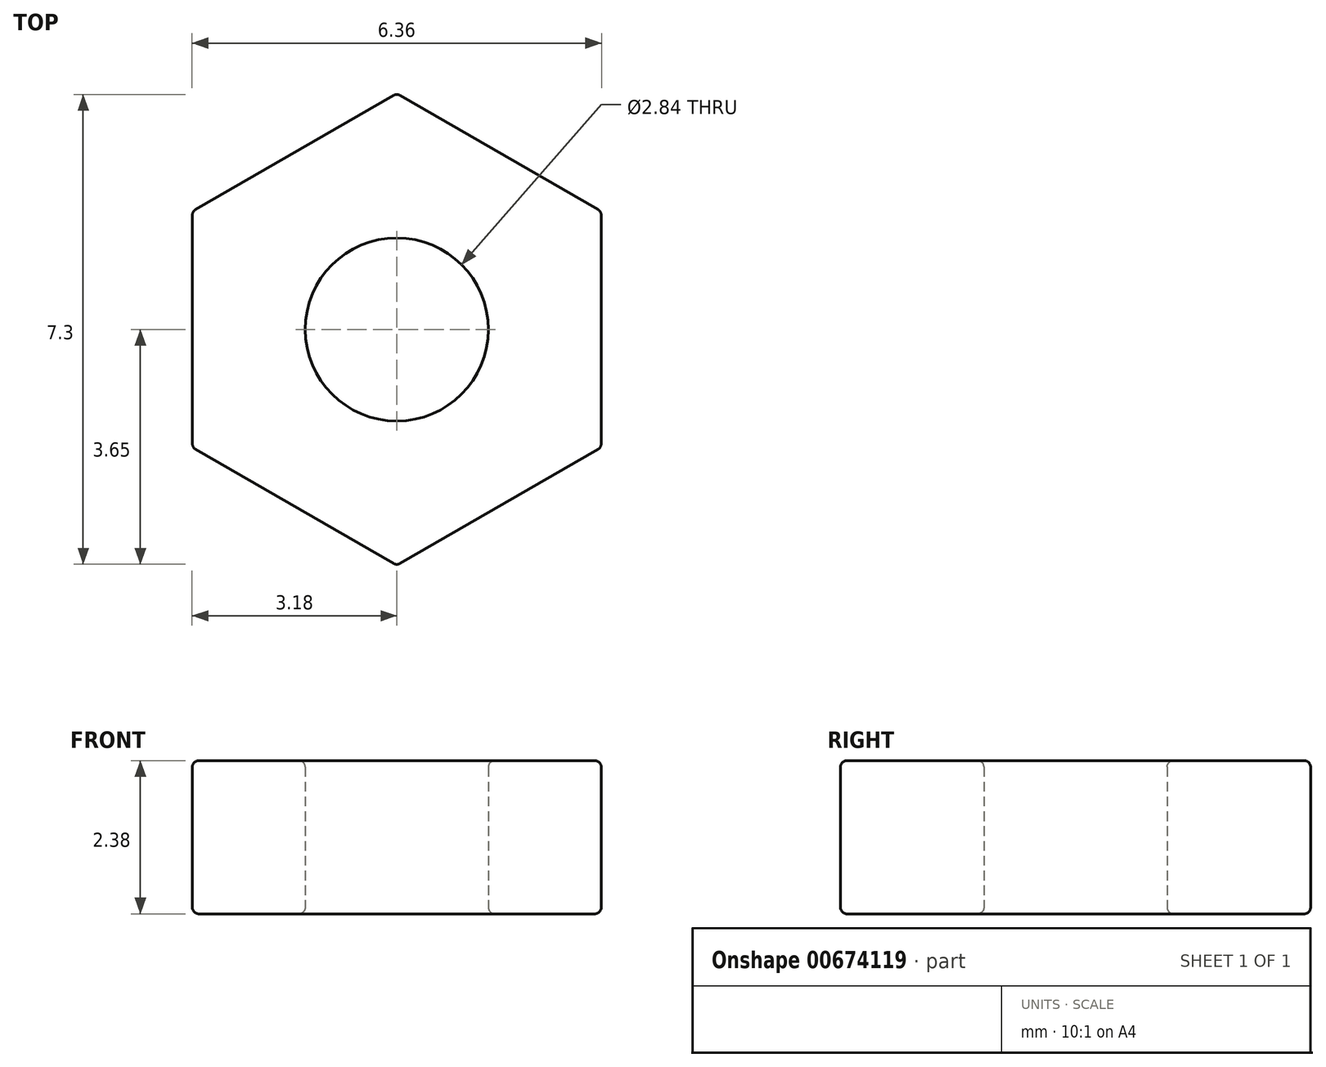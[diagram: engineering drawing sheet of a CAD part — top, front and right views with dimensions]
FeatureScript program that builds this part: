
annotation { "Feature Type Name" : "Feature", "Feature Type Description" : "" }
export const myFeature = defineFeature(function(context is Context, id is Id, definition is map)
    precondition{}
    {
        {
            var Q0;
            Q0=qCreatedBy(makeId("Top.planeOp"),FACE);
            var sketch = newSketch(context, id + "F0", { "sketchPlane" : qUnion([Q0])});
            skCircle(sketch, "E0", {"center": v(0, 0) * mm, "radius": 1.42 * mm});
            skCircle(sketch, "E1.cCircle", {"center": v(0, 0) * mm, "radius": 3.18 * mm, "construction": true});
            skLineSegment(sketch, "E1.0", {"start": v(3.18, 1.83) * mm, "end": v(3.18, -1.83) * mm});
            skLineSegment(sketch, "E1.1", {"start": v(3.18, -1.83) * mm, "end": v(0, -3.67) * mm});
            skLineSegment(sketch, "E1.2", {"start": v(0, -3.67) * mm, "end": v(-3.17, -1.83) * mm});
            skLineSegment(sketch, "E1.3", {"start": v(-3.17, -1.83) * mm, "end": v(-3.18, 1.83) * mm});
            skLineSegment(sketch, "E1.4", {"start": v(-3.18, 1.83) * mm, "end": v(0, 3.67) * mm});
            skLineSegment(sketch, "E1.5", {"start": v(0, 3.67) * mm, "end": v(3.18, 1.83) * mm});
            skPoint(sketch, "E1.0.midPoint", {"position": v(3.18, 0) * mm});
            skSolve(sketch);
        }
        {
            var Q0;
            Q0=makeQuery(id+"F0.imprint","IMPRINT",FACE,{"disambiguationData":[TD([[makeQuery(id+"F0.imprint","IMPRINT",EDGE,{"derivedFrom":sQuery(id+"F0.wireOp",EDGE,"E0")}),-1.0]])]});
            extrude(context, id + "F1", {"entities" : qUnion([Q0]), "depth" : 2.38 * mm, "offsetDistance" : 25 * mm});
        }
        {
            var Q0;
            Q0=makeQuery(id+"F1.opExtrude","SWEPT_FACE",FACE,{"disambiguationData":[OSD([sQuery(id+"F0.wireOp",EDGE,"E1.2")])]});
            var Q1;
            Q1=makeQuery(id+"F1.opExtrude","SWEPT_FACE",FACE,{"disambiguationData":[OSD([sQuery(id+"F0.wireOp",EDGE,"E1.1")])]});
            var Q2;
            Q2=makeQuery(id+"F1.opExtrude","SWEPT_FACE",FACE,{"disambiguationData":[OSD([sQuery(id+"F0.wireOp",EDGE,"E1.0")])]});
            var Q3;
            Q3=makeQuery(id+"F1.opExtrude","SWEPT_FACE",FACE,{"disambiguationData":[OSD([sQuery(id+"F0.wireOp",EDGE,"E1.5")])]});
            var Q4;
            Q4=makeQuery(id+"F1.opExtrude","SWEPT_FACE",FACE,{"disambiguationData":[OSD([sQuery(id+"F0.wireOp",EDGE,"E1.4")])]});
            var Q5;
            Q5=makeQuery(id+"F1.opExtrude","SWEPT_FACE",FACE,{"disambiguationData":[OSD([sQuery(id+"F0.wireOp",EDGE,"E1.3")])]});
            var Q6;
            Q6=makeQuery(id+"F1.opExtrude","SWEPT_FACE",FACE,{"disambiguationData":[OSD([sQuery(id+"F0.wireOp",EDGE,"E0")])]});
            fillet(context, id + "F2", {"entities" : qUnion([Q0, Q1, Q2, Q3, Q4, Q5, Q6]), "radius" : 0.1 * mm, "tangentPropagation" : true, "allowEdgeOverflow" : false});
        }
    });
